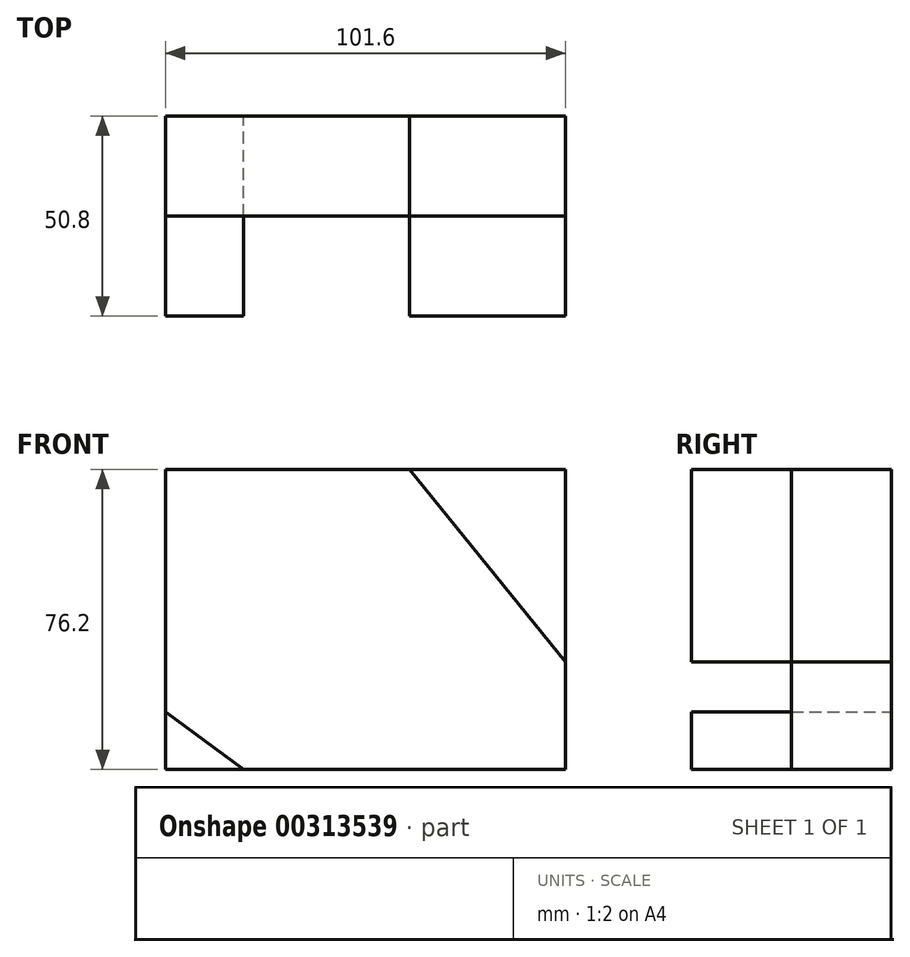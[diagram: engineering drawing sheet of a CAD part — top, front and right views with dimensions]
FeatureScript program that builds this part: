
annotation { "Feature Type Name" : "Feature", "Feature Type Description" : "" }
export const myFeature = defineFeature(function(context is Context, id is Id, definition is map)
    precondition{}
    {
        {
            var Q0;
            Q0=qCreatedBy(makeId("Front.planeOp"),FACE);
            var sketch = newSketch(context, id + "F0", { "sketchPlane" : qUnion([Q0])});
            skLineSegment(sketch, "E0.bottom", {"start": v(-51.1, 36.07) * mm, "end": v(50.5, 36.07) * mm});
            skLineSegment(sketch, "E0.top", {"start": v(-51.1, -40.13) * mm, "end": v(50.5, -40.13) * mm});
            skLineSegment(sketch, "E0.left", {"start": v(-51.1, 36.07) * mm, "end": v(-51.1, -40.13) * mm});
            skLineSegment(sketch, "E0.right", {"start": v(50.5, 36.07) * mm, "end": v(50.5, -40.13) * mm});
            skLineSegment(sketch, "E1", {"start": v(-51.1, -25.54) * mm, "end": v(-31.26, -40.13) * mm});
            skLineSegment(sketch, "E2", {"start": v(10.84, 36.07) * mm, "end": v(50.5, -12.84) * mm});
            skSolve(sketch);
        }
        {
            var Q0;
            {var subQ3=sQuery(id+"F0.wireOp",EDGE,"E2");Q0=makeQuery(id+"F0.imprint","IMPRINT",FACE,{"disambiguationData":[TD([[makeQuery(id+"F0.imprint","IMPRINT",EDGE,{"derivedFrom":subQ3}),1.0]])]});}
            var Q1;
            {var subQ3=sQuery(id+"F0.wireOp",EDGE,"E1");Q1=makeQuery(id+"F0.imprint","IMPRINT",FACE,{"disambiguationData":[TD([[makeQuery(id+"F0.imprint","IMPRINT",EDGE,{"derivedFrom":subQ3}),-1.0]])]});}
            extrude(context, id + "F1", {"entities" : qUnion([Q0, Q1]), "depth" : 50.8 * mm});
        }
        {
            var Q0;
            Q0 = qSketchRegion(id + "F0", true);
            extrude(context, id + "F2", {"entities" : qUnion([Q0]), "depth" : 25.4 * mm});
        }
    });
